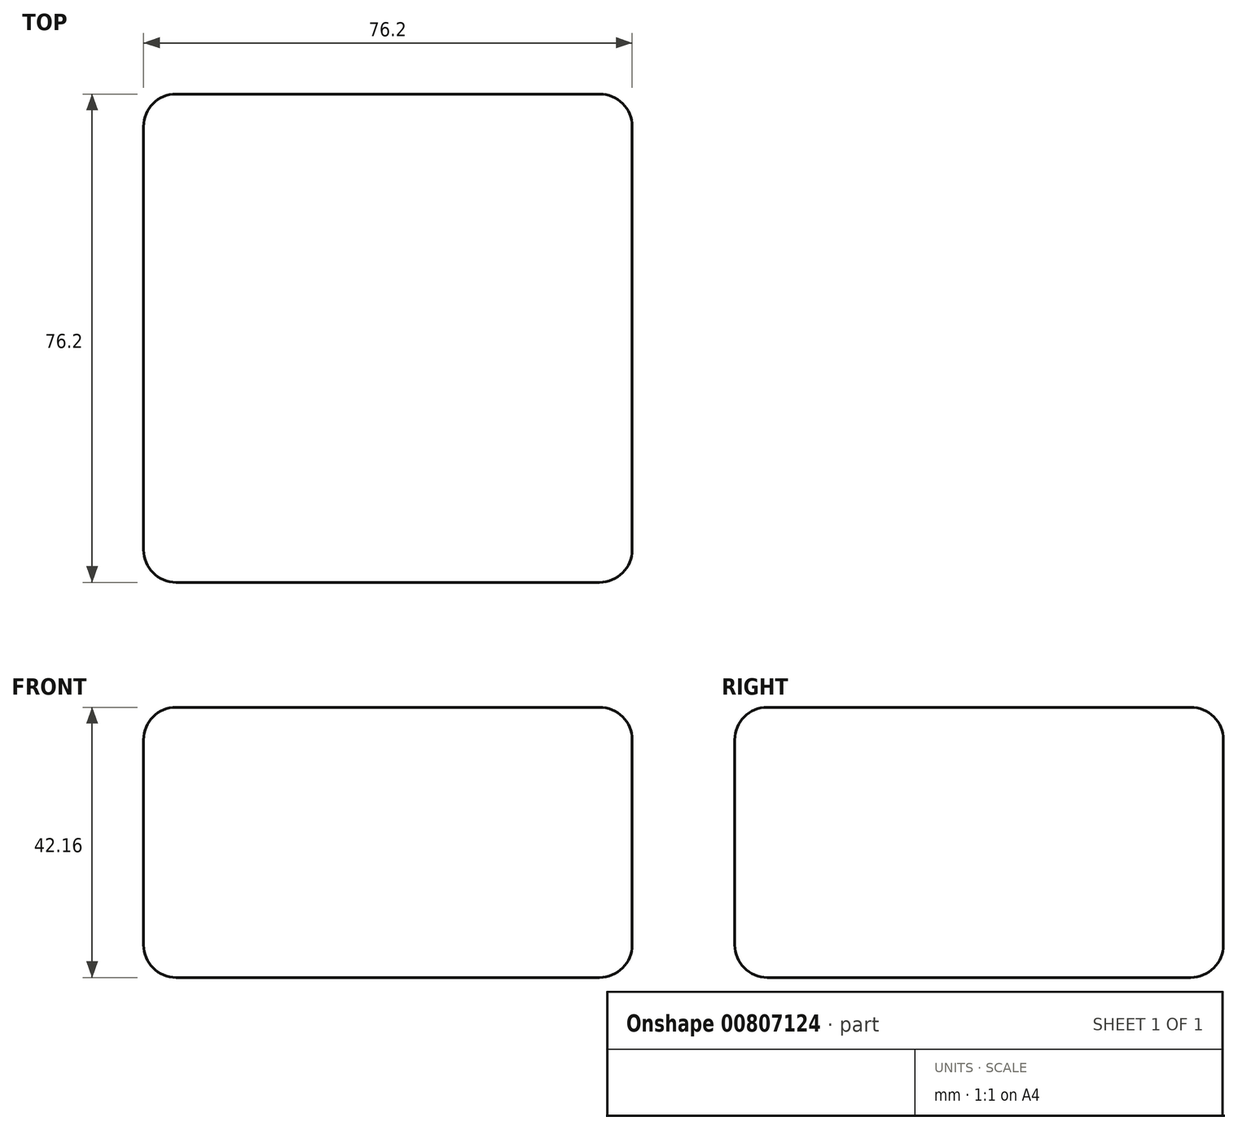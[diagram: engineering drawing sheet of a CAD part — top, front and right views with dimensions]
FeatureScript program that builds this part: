
annotation { "Feature Type Name" : "Feature", "Feature Type Description" : "" }
export const myFeature = defineFeature(function(context is Context, id is Id, definition is map)
    precondition{}
    {
        {
            var Q0;
            Q0=qCreatedBy(makeId("Top.planeOp"),FACE);
            var sketch = newSketch(context, id + "F0", { "sketchPlane" : qUnion([Q0])});
            skLineSegment(sketch, "E0.bottom", {"start": v(-79.43, 24.18) * mm, "end": v(-3.23, 24.18) * mm});
            skLineSegment(sketch, "E0.top", {"start": v(-79.43, -52.02) * mm, "end": v(-3.23, -52.02) * mm});
            skLineSegment(sketch, "E0.left", {"start": v(-79.43, 24.18) * mm, "end": v(-79.43, -52.02) * mm});
            skLineSegment(sketch, "E0.right", {"start": v(-3.23, 24.18) * mm, "end": v(-3.23, -52.02) * mm});
            skLineSegment(sketch, "E1.bottom", {"start": v(-64.78, -34.72) * mm, "end": v(-61.36, -34.72) * mm});
            skLineSegment(sketch, "E1.top", {"start": v(-64.78, -42.31) * mm, "end": v(-61.36, -42.31) * mm});
            skLineSegment(sketch, "E1.left", {"start": v(-64.78, -34.72) * mm, "end": v(-64.78, -42.31) * mm});
            skLineSegment(sketch, "E1.right", {"start": v(-61.36, -34.72) * mm, "end": v(-61.36, -42.31) * mm});
            skSolve(sketch);
        }
        {
            var Q0;
            Q0=makeQuery(id+"F0.imprint","IMPRINT",FACE,{"disambiguationData":[TD([[makeQuery(id+"F0.imprint","IMPRINT",EDGE,{"derivedFrom":sQuery(id+"F0.wireOp",EDGE,"E1.bottom")}),-1.0]])]});
            var Q1;
            Q1=makeQuery(id+"F0.imprint","IMPRINT",FACE,{"disambiguationData":[TD([[makeQuery(id+"F0.imprint","IMPRINT",EDGE,{"derivedFrom":sQuery(id+"F0.wireOp",EDGE,"E0.bottom")}),-1.0]])]});
            extrude(context, id + "F1", {"entities" : qUnion([Q0, Q1]), "depth" : 42.16 * mm, "offsetDistance" : 25.4 * mm});
        }
        {
            var Q0;
            Q0=makeQuery(id+"F1.opExtrude","CAP_FACE",FACE,{"disambiguationData":[OSD([sQuery(id+"F0.wireOp",EDGE,"E0.bottom"),sQuery(id+"F0.wireOp",EDGE,"E0.top"),sQuery(id+"F0.wireOp",EDGE,"E0.left"),sQuery(id+"F0.wireOp",EDGE,"E0.right")])],"isStart":true});
            var Q1;
            Q1=makeQuery(id+"F1.opExtrude","SWEPT_FACE",FACE,{"disambiguationData":[OSD([sQuery(id+"F0.wireOp",EDGE,"E0.left")])]});
            var Q2;
            Q2=makeQuery(id+"F1.opExtrude","CAP_FACE",FACE,{"disambiguationData":[OSD([sQuery(id+"F0.wireOp",EDGE,"E0.bottom"),sQuery(id+"F0.wireOp",EDGE,"E0.top"),sQuery(id+"F0.wireOp",EDGE,"E0.left"),sQuery(id+"F0.wireOp",EDGE,"E0.right")])],"isStart":false});
            var Q3;
            Q3=makeQuery(id+"F1.opExtrude","SWEPT_FACE",FACE,{"disambiguationData":[OSD([sQuery(id+"F0.wireOp",EDGE,"E0.bottom")])]});
            fillet(context, id + "F2", {"entities" : qUnion([Q0, Q1, Q2, Q3]), "radius" : 5.08 * mm, "tangentPropagation" : true, "allowEdgeOverflow" : false});
        }
        {
            var Q0;
            Q0=makeQuery(id+"F1.opExtrude","SWEPT_EDGE",EDGE,{"disambiguationData":[OSD([sQuery(id+"F0.wireOp",EDGE,"E0.top"),sQuery(id+"F0.wireOp",EDGE,"E0.right")])]});
            fillet(context, id + "F3", {"entities" : qUnion([Q0]), "radius" : 5.08 * mm, "tangentPropagation" : true, "allowEdgeOverflow" : false});
        }
    });
